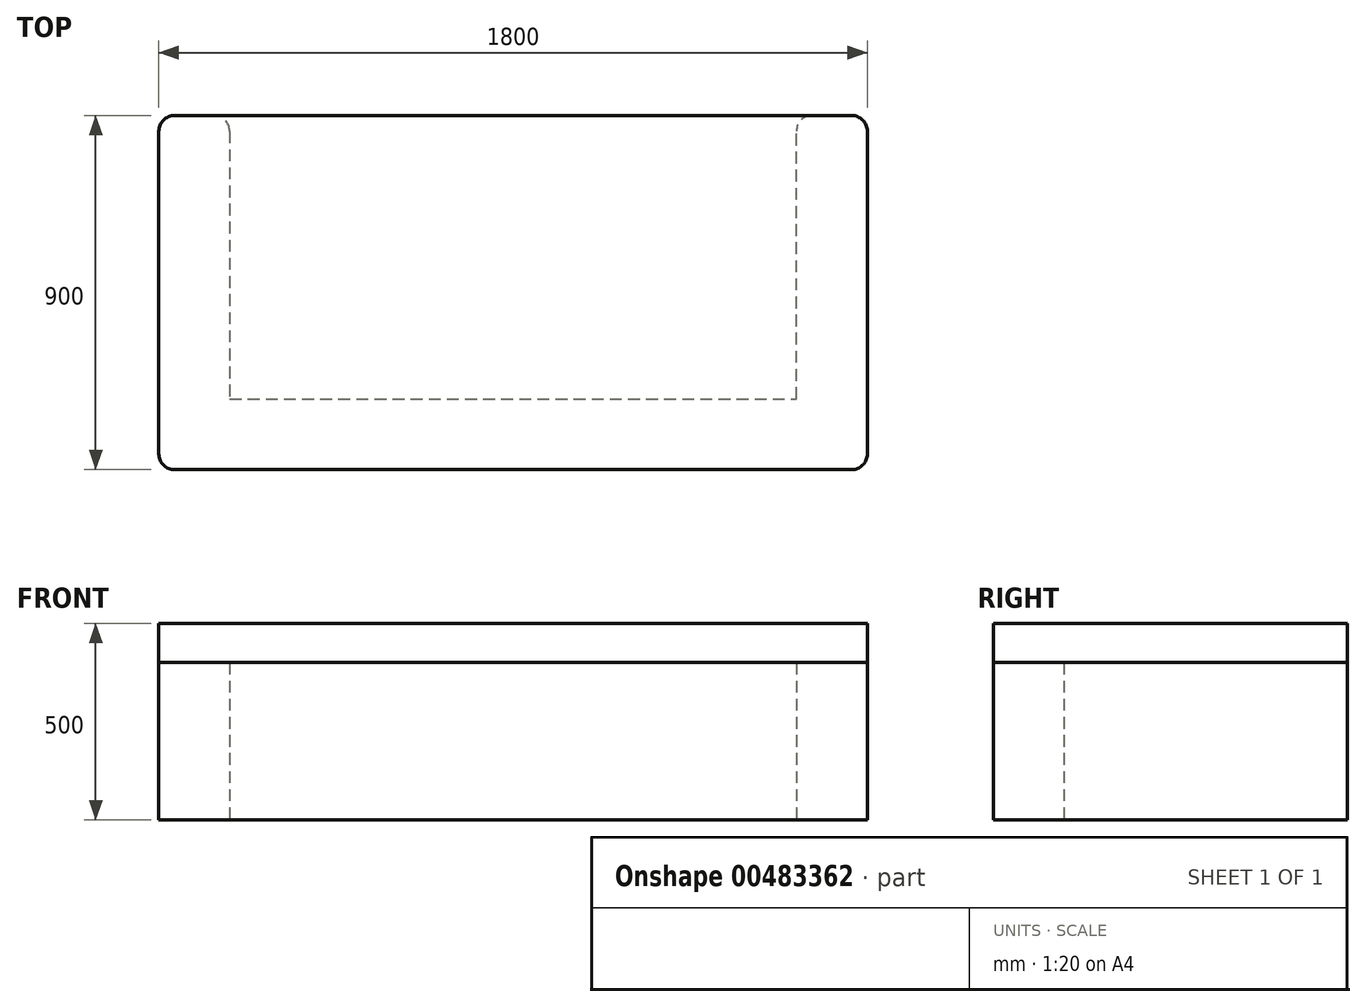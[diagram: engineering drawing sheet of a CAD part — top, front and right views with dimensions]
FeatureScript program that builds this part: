
annotation { "Feature Type Name" : "Feature", "Feature Type Description" : "" }
export const myFeature = defineFeature(function(context is Context, id is Id, definition is map)
    precondition{}
    {
        {
            var Q0;
            Q0=qCreatedBy(makeId("Top.planeOp"),FACE);
            var sketch = newSketch(context, id + "F0", { "sketchPlane" : qUnion([Q0])});
            skLineSegment(sketch, "E0", {"start": v(40, 0) * mm, "end": v(1760, 0) * mm});
            skLineSegment(sketch, "E1", {"start": v(1800, 40) * mm, "end": v(1800, 860) * mm});
            skLineSegment(sketch, "E2", {"start": v(1760, 900) * mm, "end": v(40, 900) * mm});
            skLineSegment(sketch, "E3", {"start": v(0, 860) * mm, "end": v(0, 40) * mm});
            skPoint(sketch, "E4.visualSharp", {"position": v(0, 900) * mm});
            skArc(sketch, "E4.filletArc", {"start": v(40, 900) * mm, "mid": v(11.72, 888.28) * mm, "end": v(0, 860) * mm});
            skPoint(sketch, "E5.visualSharp", {"position": v(0, 0) * mm});
            skArc(sketch, "E5.filletArc", {"start": v(0, 40) * mm, "mid": v(11.72, 11.72) * mm, "end": v(40, 0) * mm});
            skPoint(sketch, "E6.visualSharp", {"position": v(1800, 0) * mm});
            skArc(sketch, "E6.filletArc", {"start": v(1760, 0) * mm, "mid": v(1788.28, 11.72) * mm, "end": v(1800, 40) * mm});
            skPoint(sketch, "E7.visualSharp", {"position": v(1800, 900) * mm});
            skArc(sketch, "E7.filletArc", {"start": v(1800, 860) * mm, "mid": v(1788.28, 888.28) * mm, "end": v(1760, 900) * mm});
            skSolve(sketch);
        }
        {
            var Q0;
            Q0=makeQuery(id+"F0.imprint","IMPRINT",FACE,{"disambiguationData":[TD([[makeQuery(id+"F0.imprint","IMPRINT",EDGE,{"derivedFrom":sQuery(id+"F0.wireOp",EDGE,"E0")}),1.0]])]});
            var Q1;
            Q1 = qSketchRegion(id + "F2", true);
            extrude(context, id + "F1", {"entities" : qUnion([Q0, Q1]), "depth" : 500 * mm});
        }
        {
            var Q0;
            Q0=qCreatedBy(makeId("Top.planeOp"),FACE);
            var sketch = newSketch(context, id + "F2", { "sketchPlane" : qUnion([Q0])});
            skLineSegment(sketch, "E8.0", {"start": v(0, 860) * mm, "end": v(0, 40) * mm});
            skPoint(sketch, "E9.newPointA", {"position": v(40, 900) * mm});
            skPoint(sketch, "E9.newPointB", {"position": v(0, 860) * mm});
            skArc(sketch, "E9.filletArc", {"start": v(40, 900) * mm, "mid": v(11.72, 888.28) * mm, "end": v(0, 860) * mm});
            skLineSegment(sketch, "E10.0", {"start": v(40, 0) * mm, "end": v(1760, 0) * mm});
            skLineSegment(sketch, "E11.0", {"start": v(1800, 40) * mm, "end": v(1800, 860) * mm});
            skPoint(sketch, "E12.newPointB", {"position": v(40, 0) * mm});
            skArc(sketch, "E12.filletArc", {"start": v(0, 40) * mm, "mid": v(11.72, 11.72) * mm, "end": v(40, 0) * mm});
            skPoint(sketch, "E13.newPointA", {"position": v(1800, 40) * mm});
            skPoint(sketch, "E13.newPointB", {"position": v(1760, 0) * mm});
            skArc(sketch, "E13.filletArc", {"start": v(1760, 0) * mm, "mid": v(1788.28, 11.72) * mm, "end": v(1800, 40) * mm});
            skPoint(sketch, "E14.newPointB", {"position": v(1800, 860) * mm});
            skLineSegment(sketch, "E15", {"start": v(40, 900) * mm, "end": v(140, 900) * mm});
            skLineSegment(sketch, "E16", {"start": v(180, 860) * mm, "end": v(180, 180) * mm});
            skLineSegment(sketch, "E17", {"start": v(180, 180) * mm, "end": v(1620, 180) * mm});
            skPoint(sketch, "E18.visualSharp", {"position": v(180, 900) * mm});
            skArc(sketch, "E18.filletArc", {"start": v(180, 860) * mm, "mid": v(168.28, 888.28) * mm, "end": v(140, 900) * mm});
            skLineSegment(sketch, "E19", {"start": v(1620, 180) * mm, "end": v(1620, 860) * mm});
            skLineSegment(sketch, "E20", {"start": v(1760, 900) * mm, "end": v(1660, 900) * mm});
            skPoint(sketch, "E21.visualSharp", {"position": v(1800, 900) * mm});
            skPoint(sketch, "E22.visualSharp", {"position": v(1620, 900) * mm});
            skArc(sketch, "E22.filletArc", {"start": v(1660, 900) * mm, "mid": v(1631.72, 888.28) * mm, "end": v(1620, 860) * mm});
            skPoint(sketch, "E23.newPointB", {"position": v(1800, 900.57) * mm});
            skArc(sketch, "E23.filletArc", {"start": v(1800, 860) * mm, "mid": v(1788.28, 888.28) * mm, "end": v(1760, 900) * mm});
            skSolve(sketch);
        }
        {
            var Q0;
            Q0=makeQuery(id+"F2.imprint","IMPRINT",FACE,{"disambiguationData":[TD([[makeQuery(id+"F2.imprint","IMPRINT",EDGE,{"derivedFrom":sQuery(id+"F2.wireOp",EDGE,"E8.0")}),1.0]])]});
            extrude(context, id + "F3", {"entities" : qUnion([Q0]), "depth" : 400 * mm});
        }
    });
